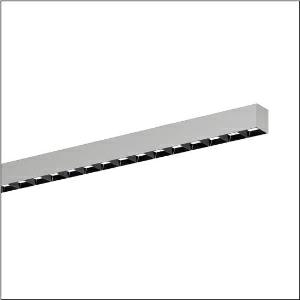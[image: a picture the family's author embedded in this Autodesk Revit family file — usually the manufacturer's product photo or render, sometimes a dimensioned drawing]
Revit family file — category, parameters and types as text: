
# Revit family: silica_r__21_51mx21tctas_c3b1
name_source: partatom
category: Lighting Fixtures
units: mm (PartAtom-declared; Revit-internal decimal feet)

## family parameters
Cut with Voids When Loaded = No
Host = Face
Light Source = No
Part Type = Normal
Room Calculation Point = No
Round Connector Dimension = Use Diameter
Shared = No

## types (1)
- --- (1 x LED, 9300 lm, 80.5 W, 6500K)
    Apparent Load = 81 VA
    CIE Flux Codes = 85 99 100 100 100
    Color Rendering = 80
    Color Temperature = 6500K
    Default Elevation = 1800 mm
    Description = Silica® 21, office luminaire, primary light control with darklight reflector, of PMMA, black, CAT 2 (L<= 3000cd/m²), light emission: direct distribution, primary light characteristic: symmetric, installation type: surface-mounted, LED, rated luminous flux: 9.300lm, luminous efficacy: 110lm/W, light colour: 8tw, colour temperature: 2700..6500K, control gear: ECG DALI, with terminal, 3+2-pole, max. 2.5mm², mains connection: 220..240V, AC, 50/60Hz, rated input power: 84.6W, luminaire housing, of aluminium, metallic grey (RAL 9006), length: 3.004mm, width: 53mm, height: 53mm, protection rating (complete): IP20, insulation class (complete): insulation class I (protective earthing), certification: CE, permissible operating ambient temperature: 0..+35°C, standard: EN 50419, packaging unit: 1 piece
    Height = 0 mm  [stored 0 ft]
    Lamp = 1 x LED
    Lamp Light Flux = 9300 lm
    Lamp Power = 80.5 W
    Lamp count = 1
    Length = 3004 mm
    Luminous efficacy = 116 lm/W
    Manufacturer = Siteco
    ModVariant = No
    Model = 51MX21TCTAS
    Mounting Place = Ceiling
    Mounting Type = Recessed
    Number of Poles = 1
    OnlyDefault = Yes
    Power Factor = 1
    Product Name = Silica® 21
    Product group = office luminaire | ceiling recessed
    ProductGroupID = 401
    Protection Class = Protection class I
    Protection Degree = IP 20
    RLX_Detail_Level = 1
    RLX_Emergency_Light_Flux = 0 lm
    RLX_Emergency_Type = 0
    RLX_Emergency_Type_DB = No
    RlxData = <blob elided: 60481 chars, md5=bd8e96c9>
    Socket = socket
    Standby Power = 0 W
    System Light Flux = 9300 lm
    System Power = 81 W
    Type Comments = individual setting
    Type Image = l_1297764.jpg
    URL = http://relux.com
    VarID = @adj_071365
    Voltage = 0 V
    Weight = 0.00 kg
    Width = 53 mm

note: [stored X ft] marks values corroborated as IEEE doubles in the binary element streams (Revit-internal decimal feet)

## geometry (parser evidence)
native form markers: Blend x4, Sweep x10
no freeform markers — native parametric forms only
